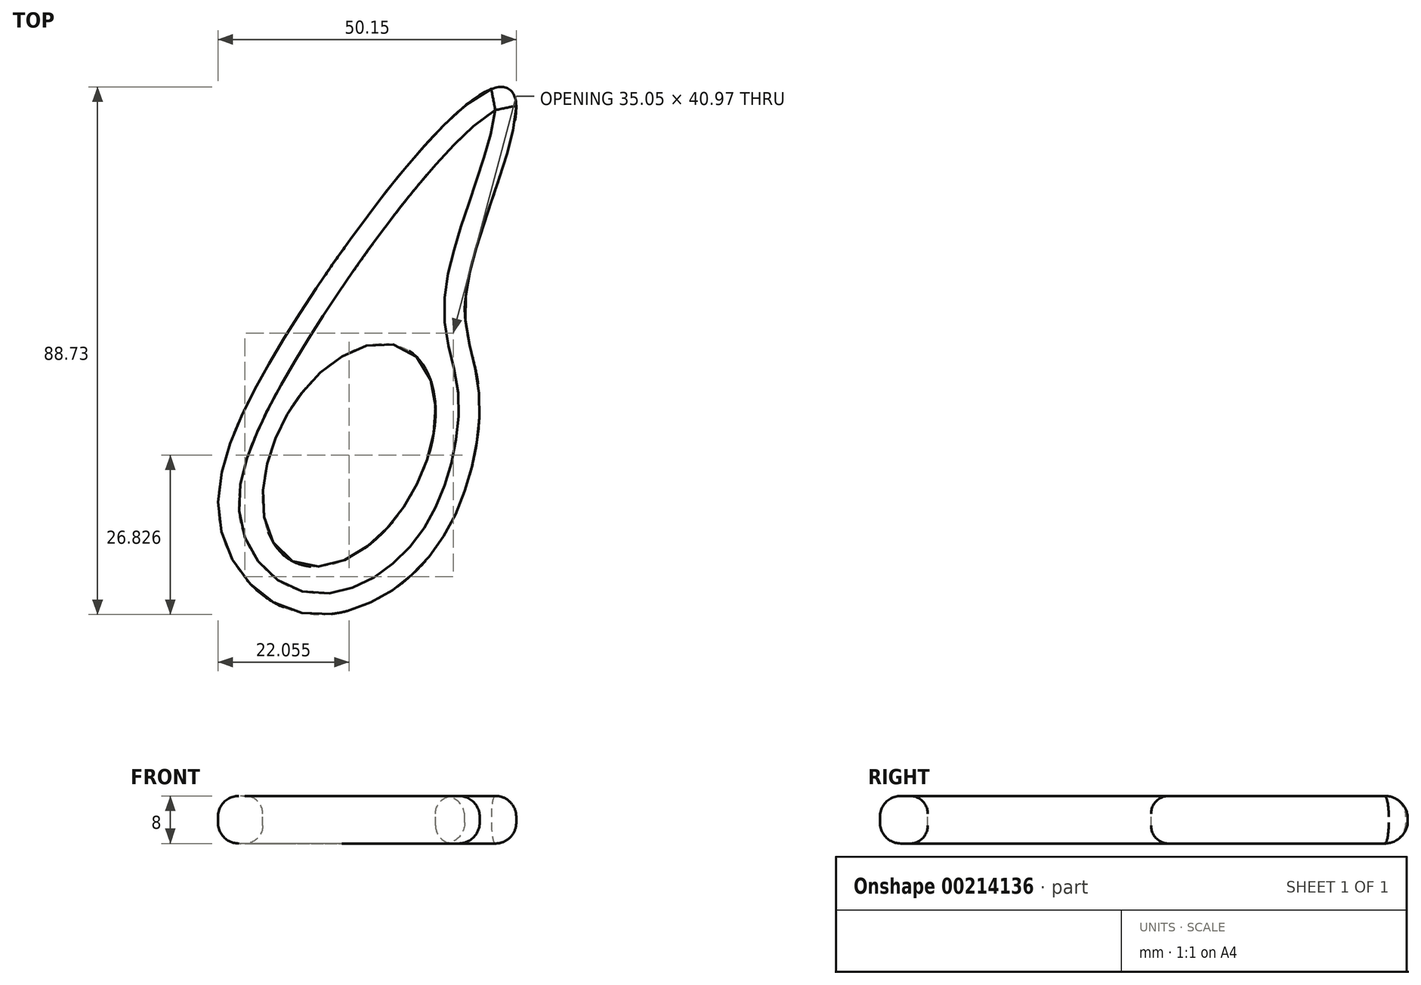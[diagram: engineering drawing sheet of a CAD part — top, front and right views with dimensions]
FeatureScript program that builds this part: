
annotation { "Feature Type Name" : "Feature", "Feature Type Description" : "" }
export const myFeature = defineFeature(function(context is Context, id is Id, definition is map)
    precondition{}
    {
        {
            var Q0;
            Q0=qCreatedBy(makeId("Top.planeOp"),FACE);
            var sketch = newSketch(context, id + "F0", { "sketchPlane" : qUnion([Q0])});
            skFitSpline(sketch, "E0", {"points": [v(43.67, -64.16) * mm, v(60.6, -51.9) * mm, v(66.82, -26.42) * mm, v(64.68, -10.47) * mm, v(73.07, 21.8) * mm, v(68.7, 23.77) * mm, v(32.08, -21.49) * mm, v(23.25, -49.18) * mm, v(30.97, -61.58) * mm, v(43.67, -64.16) * mm]});
            skEllipse(sketch, "E1", {"center": v(45.04, -37.7) * mm, "majorRadius": 20.23 * mm, "minorRadius": 12.4 * mm, "majorAxis": v(-0.47, -0.88)});
            skSolve(sketch);
        }
        {
            var Q0;
            Q0=makeQuery(id+"F0.imprint","IMPRINT",FACE,{"disambiguationData":[TD([[makeQuery(id+"F0.imprint","IMPRINT",EDGE,{"derivedFrom":sQuery(id+"F0.wireOp",EDGE,"E0")}),1.0]])]});
            extrude(context, id + "F1", {"entities" : qUnion([Q0]), "depth" : 8 * mm});
        }
        {
            var Q0;
            Q0=makeQuery(id+"F1.opExtrude","CAP_EDGE",EDGE,{"disambiguationData":[OSD([sQuery(id+"F0.wireOp",EDGE,"E0")])],"isStart":false});
            fillet(context, id + "F2", {"entities" : qUnion([Q0]), "radius" : 3.5 * mm, "tangentPropagation" : true, "allowEdgeOverflow" : false});
        }
        {
            var Q0;
            Q0=makeQuery(id+"F1.opExtrude","CAP_EDGE",EDGE,{"disambiguationData":[OSD([sQuery(id+"F0.wireOp",EDGE,"E0")])],"isStart":true});
            fillet(context, id + "F3", {"entities" : qUnion([Q0]), "radius" : 3.5 * mm, "tangentPropagation" : true, "allowEdgeOverflow" : false});
        }
        {
            var Q0;
            Q0=makeQuery(id+"F1.opExtrude","CAP_EDGE",EDGE,{"disambiguationData":[OSD([sQuery(id+"F0.wireOp",EDGE,"E1")])],"isStart":false});
            fillet(context, id + "F4", {"entities" : qUnion([Q0]), "radius" : 3 * mm, "tangentPropagation" : true, "allowEdgeOverflow" : false});
        }
        {
            var Q0;
            Q0=makeQuery(id+"F1.opExtrude","CAP_EDGE",EDGE,{"disambiguationData":[OSD([sQuery(id+"F0.wireOp",EDGE,"E1")])],"isStart":true});
            fillet(context, id + "F5", {"entities" : qUnion([Q0]), "radius" : 3 * mm, "tangentPropagation" : true, "allowEdgeOverflow" : false});
        }
    });
